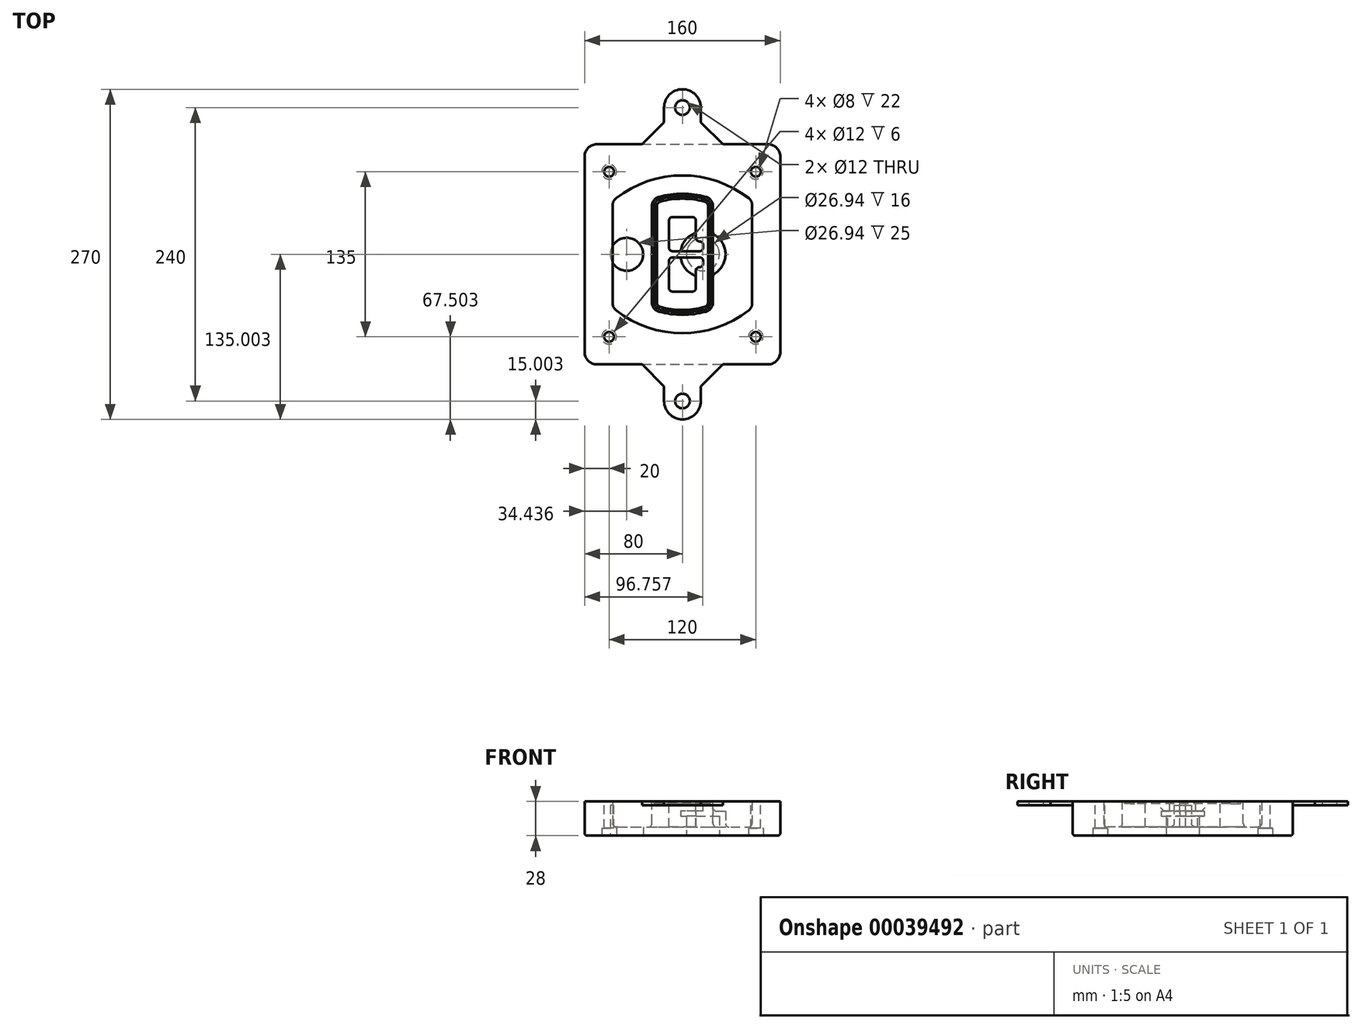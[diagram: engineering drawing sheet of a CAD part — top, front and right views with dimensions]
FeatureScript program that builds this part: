
annotation { "Feature Type Name" : "Feature", "Feature Type Description" : "" }
export const myFeature = defineFeature(function(context is Context, id is Id, definition is map)
    precondition{}
    {
        {
            var Q0;
            Q0=qCreatedBy(makeId("Top.planeOp"),FACE);
            var sketch = newSketch(context, id + "F0", { "sketchPlane" : qUnion([Q0])});
            skPoint(sketch, "E0.rect.middle", {"position": v(0, 0) * mm});
            skLineSegment(sketch, "E1.bottom", {"start": v(24.05, 28.38) * mm, "end": v(164.05, 28.38) * mm});
            skLineSegment(sketch, "E1.top", {"start": v(24.05, 208.38) * mm, "end": v(164.05, 208.38) * mm});
            skLineSegment(sketch, "E1.left", {"start": v(14.05, 38.38) * mm, "end": v(14.05, 198.38) * mm});
            skLineSegment(sketch, "E1.right", {"start": v(174.05, 38.38) * mm, "end": v(174.05, 198.38) * mm});
            skLineSegment(sketch, "E2", {"start": v(14.05, 208.38) * mm, "end": v(174.05, 28.38) * mm, "construction": true});
            skLineSegment(sketch, "E3", {"start": v(174.05, 208.38) * mm, "end": v(14.05, 28.38) * mm, "construction": true});
            skCircle(sketch, "E4", {"center": v(34.05, 185.88) * mm, "radius": 4 * mm});
            skCircle(sketch, "E5", {"center": v(154.05, 185.88) * mm, "radius": 4 * mm});
            skCircle(sketch, "E6", {"center": v(154.05, 50.88) * mm, "radius": 4 * mm});
            skCircle(sketch, "E7", {"center": v(34.05, 50.88) * mm, "radius": 4 * mm});
            skLineSegment(sketch, "E8", {"start": v(34.05, 185.88) * mm, "end": v(154.05, 185.88) * mm, "construction": true});
            skLineSegment(sketch, "E9", {"start": v(154.05, 185.88) * mm, "end": v(154.05, 50.88) * mm, "construction": true});
            skLineSegment(sketch, "E10", {"start": v(154.05, 50.88) * mm, "end": v(34.05, 50.88) * mm, "construction": true});
            skLineSegment(sketch, "E11", {"start": v(34.05, 50.88) * mm, "end": v(34.05, 185.88) * mm, "construction": true});
            skLineSegment(sketch, "E12", {"start": v(34.05, 158.68) * mm, "end": v(34.05, 78.09) * mm});
            skLineSegment(sketch, "E13", {"start": v(154.05, 158.68) * mm, "end": v(154.05, 78.09) * mm});
            skArc(sketch, "E14", {"start": v(150.2, 166.56) * mm, "mid": v(94.05, 185.88) * mm, "end": v(37.9, 166.56) * mm});
            skArc(sketch, "E15", {"start": v(37.9, 70.2) * mm, "mid": v(94.05, 50.88) * mm, "end": v(150.2, 70.2) * mm});
            skLineSegment(sketch, "E16", {"start": v(34.05, 118.38) * mm, "end": v(154.05, 118.38) * mm, "construction": true});
            skPoint(sketch, "E17.visualSharp", {"position": v(34.05, 73.38) * mm});
            skArc(sketch, "E17.filletArc", {"start": v(34.05, 78.09) * mm, "mid": v(35.06, 73.7) * mm, "end": v(37.9, 70.2) * mm});
            skPoint(sketch, "E18.visualSharp", {"position": v(34.05, 163.38) * mm});
            skArc(sketch, "E18.filletArc", {"start": v(37.9, 166.56) * mm, "mid": v(35.06, 163.06) * mm, "end": v(34.05, 158.68) * mm});
            skPoint(sketch, "E19.visualSharp", {"position": v(154.05, 163.38) * mm});
            skArc(sketch, "E19.filletArc", {"start": v(154.05, 158.68) * mm, "mid": v(153.04, 163.06) * mm, "end": v(150.2, 166.56) * mm});
            skPoint(sketch, "E20.visualSharp", {"position": v(154.05, 73.38) * mm});
            skArc(sketch, "E20.filletArc", {"start": v(150.2, 70.2) * mm, "mid": v(153.04, 73.7) * mm, "end": v(154.05, 78.09) * mm});
            skPoint(sketch, "E21.visualSharp", {"position": v(14.05, 208.38) * mm});
            skArc(sketch, "E21.filletArc", {"start": v(24.05, 208.38) * mm, "mid": v(16.98, 205.45) * mm, "end": v(14.05, 198.38) * mm});
            skPoint(sketch, "E22.visualSharp", {"position": v(174.05, 208.38) * mm});
            skArc(sketch, "E22.filletArc", {"start": v(174.05, 198.38) * mm, "mid": v(171.12, 205.45) * mm, "end": v(164.05, 208.38) * mm});
            skPoint(sketch, "E23.visualSharp", {"position": v(174.05, 28.38) * mm});
            skArc(sketch, "E23.filletArc", {"start": v(164.05, 28.38) * mm, "mid": v(171.12, 31.31) * mm, "end": v(174.05, 38.38) * mm});
            skPoint(sketch, "E24.visualSharp", {"position": v(14.05, 28.38) * mm});
            skArc(sketch, "E24.filletArc", {"start": v(14.05, 38.38) * mm, "mid": v(16.98, 31.31) * mm, "end": v(24.05, 28.38) * mm});
            skArc(sketch, "E25.0", {"start": v(151.05, 158.68) * mm, "mid": v(150.34, 161.75) * mm, "end": v(148.36, 164.2) * mm});
            skLineSegment(sketch, "E25.1", {"start": v(151.05, 158.68) * mm, "end": v(151.05, 78.09) * mm});
            skArc(sketch, "E25.2", {"start": v(148.36, 72.57) * mm, "mid": v(150.34, 75.02) * mm, "end": v(151.05, 78.09) * mm});
            skArc(sketch, "E25.3", {"start": v(39.74, 72.57) * mm, "mid": v(94.05, 53.88) * mm, "end": v(148.36, 72.57) * mm});
            skArc(sketch, "E25.4", {"start": v(37.05, 78.09) * mm, "mid": v(37.76, 75.02) * mm, "end": v(39.74, 72.57) * mm});
            skArc(sketch, "E25.5", {"start": v(148.36, 164.2) * mm, "mid": v(94.05, 182.88) * mm, "end": v(39.74, 164.2) * mm});
            skLineSegment(sketch, "E25.6", {"start": v(37.05, 158.68) * mm, "end": v(37.05, 78.09) * mm});
            skArc(sketch, "E25.7", {"start": v(39.74, 164.2) * mm, "mid": v(37.76, 161.75) * mm, "end": v(37.05, 158.68) * mm});
            skArc(sketch, "E26.0", {"start": v(35.43, 169.71) * mm, "mid": v(31.47, 164.82) * mm, "end": v(30.05, 158.68) * mm});
            skArc(sketch, "E26.1", {"start": v(152.67, 169.71) * mm, "mid": v(94.05, 189.88) * mm, "end": v(35.43, 169.71) * mm});
            skArc(sketch, "E26.2", {"start": v(158.05, 158.68) * mm, "mid": v(156.63, 164.82) * mm, "end": v(152.67, 169.71) * mm});
            skLineSegment(sketch, "E26.3", {"start": v(158.05, 158.68) * mm, "end": v(158.05, 78.09) * mm});
            skArc(sketch, "E26.4", {"start": v(152.67, 67.05) * mm, "mid": v(156.63, 71.95) * mm, "end": v(158.05, 78.09) * mm});
            skLineSegment(sketch, "E26.5", {"start": v(30.05, 158.68) * mm, "end": v(30.05, 78.09) * mm});
            skArc(sketch, "E26.6", {"start": v(35.43, 67.05) * mm, "mid": v(94.05, 46.88) * mm, "end": v(152.67, 67.05) * mm});
            skArc(sketch, "E26.7", {"start": v(30.05, 78.09) * mm, "mid": v(31.47, 71.95) * mm, "end": v(35.43, 67.05) * mm});
            skSolve(sketch);
        }
        {
            var Q0;
            Q0=makeQuery(id+"F0.imprint","IMPRINT",FACE,{"disambiguationData":[TD([[makeQuery(id+"F0.imprint","IMPRINT",EDGE,{"derivedFrom":sQuery(id+"F0.wireOp",EDGE,"E1.bottom")}),1.0]])]});
            var Q1;
            Q1=makeQuery(id+"F0.imprint","IMPRINT",FACE,{"disambiguationData":[TD([[makeQuery(id+"F0.imprint","IMPRINT",EDGE,{"derivedFrom":sQuery(id+"F0.wireOp",EDGE,"E12")}),1.0]])]});
            var Q2;
            Q2=makeQuery(id+"F0.imprint","IMPRINT",FACE,{"disambiguationData":[TD([[makeQuery(id+"F0.imprint","IMPRINT",EDGE,{"derivedFrom":sQuery(id+"F0.wireOp",EDGE,"E25.0")}),1.0]])]});
            var Q3;
            Q3=makeQuery(id+"F0.imprint","IMPRINT",FACE,{"disambiguationData":[TD([[makeQuery(id+"F0.imprint","IMPRINT",EDGE,{"derivedFrom":sQuery(id+"F0.wireOp",EDGE,"E12")}),-1.0]])]});
            extrude(context, id + "F1", {"entities" : qUnion([Q0, Q1, Q2, Q3]), "oppositeDirection" : true, "depth" : 25 * mm});
        }
        {
            var Q0;
            Q0=makeQuery(id+"F0.imprint","IMPRINT",FACE,{"disambiguationData":[TD([[makeQuery(id+"F0.imprint","IMPRINT",EDGE,{"derivedFrom":sQuery(id+"F0.wireOp",EDGE,"E12")}),1.0]])]});
            extrude(context, id + "F2", {"entities" : qUnion([Q0]), "operationType" : NewBodyOperationType.ADD, "depth" : 3 * mm});
        }
        {
            var Q0;
            Q0=makeQuery(id+"F0.imprint","IMPRINT",FACE,{"disambiguationData":[TD([[makeQuery(id+"F0.imprint","IMPRINT",EDGE,{"derivedFrom":sQuery(id+"F0.wireOp",EDGE,"E25.0")}),1.0]])]});
            extrude(context, id + "F3", {"entities" : qUnion([Q0]), "operationType" : NewBodyOperationType.REMOVE, "oppositeDirection" : true, "depth" : 18 * mm});
        }
        {
            var Q0;
            Q0=makeQuery(id+"F2.opExtrude","CAP_FACE",FACE,{"disambiguationData":[OSD([sQuery(id+"F0.wireOp",EDGE,"E12"),sQuery(id+"F0.wireOp",EDGE,"E13"),sQuery(id+"F0.wireOp",EDGE,"E14"),sQuery(id+"F0.wireOp",EDGE,"E15"),sQuery(id+"F0.wireOp",EDGE,"E17.filletArc"),sQuery(id+"F0.wireOp",EDGE,"E18.filletArc"),sQuery(id+"F0.wireOp",EDGE,"E19.filletArc"),sQuery(id+"F0.wireOp",EDGE,"E20.filletArc"),sQuery(id+"F0.wireOp",EDGE,"E25.0"),sQuery(id+"F0.wireOp",EDGE,"E25.1"),sQuery(id+"F0.wireOp",EDGE,"E25.2"),sQuery(id+"F0.wireOp",EDGE,"E25.3"),sQuery(id+"F0.wireOp",EDGE,"E25.4"),sQuery(id+"F0.wireOp",EDGE,"E25.5"),sQuery(id+"F0.wireOp",EDGE,"E25.6"),sQuery(id+"F0.wireOp",EDGE,"E25.7")])],"isStart":false});
            var sketch = newSketch(context, id + "F4", { "sketchPlane" : qUnion([Q0])});
            skArc(sketch, "E27.0", {"start": v(74.97, 71.41) * mm, "mid": v(94.05, 68.88) * mm, "end": v(113.13, 71.41) * mm});
            skArc(sketch, "E28.0", {"start": v(113.13, 165.35) * mm, "mid": v(94.05, 167.88) * mm, "end": v(74.97, 165.35) * mm});
            skLineSegment(sketch, "E29", {"start": v(69.05, 157.63) * mm, "end": v(69.05, 79.14) * mm});
            skLineSegment(sketch, "E30", {"start": v(119.05, 157.63) * mm, "end": v(119.05, 79.14) * mm});
            skLineSegment(sketch, "E31", {"start": v(69.05, 163.48) * mm, "end": v(119.05, 163.48) * mm, "construction": true});
            skLineSegment(sketch, "E32", {"start": v(69.05, 73.28) * mm, "end": v(119.05, 73.28) * mm, "construction": true});
            skPoint(sketch, "E33.visualSharp", {"position": v(69.05, 163.48) * mm});
            skArc(sketch, "E33.filletArc", {"start": v(74.97, 165.35) * mm, "mid": v(70.7, 162.5) * mm, "end": v(69.05, 157.63) * mm});
            skPoint(sketch, "E34.visualSharp", {"position": v(119.05, 163.48) * mm});
            skArc(sketch, "E34.filletArc", {"start": v(119.05, 157.63) * mm, "mid": v(117.4, 162.5) * mm, "end": v(113.13, 165.35) * mm});
            skPoint(sketch, "E35.visualSharp", {"position": v(119.05, 73.28) * mm});
            skArc(sketch, "E35.filletArc", {"start": v(113.13, 71.41) * mm, "mid": v(117.4, 74.27) * mm, "end": v(119.05, 79.14) * mm});
            skPoint(sketch, "E36.visualSharp", {"position": v(69.05, 73.28) * mm});
            skArc(sketch, "E36.filletArc", {"start": v(69.05, 79.14) * mm, "mid": v(70.7, 74.27) * mm, "end": v(74.97, 71.41) * mm});
            skArc(sketch, "E37.0", {"start": v(148.36, 164.2) * mm, "mid": v(94.05, 182.88) * mm, "end": v(39.74, 164.2) * mm});
            skArc(sketch, "E37.1", {"start": v(39.74, 164.2) * mm, "mid": v(37.76, 161.75) * mm, "end": v(37.05, 158.68) * mm});
            skLineSegment(sketch, "E37.2", {"start": v(37.05, 158.68) * mm, "end": v(37.05, 78.09) * mm});
            skArc(sketch, "E37.3", {"start": v(37.05, 78.09) * mm, "mid": v(37.76, 75.02) * mm, "end": v(39.74, 72.57) * mm});
            skArc(sketch, "E37.4", {"start": v(39.74, 72.57) * mm, "mid": v(94.05, 53.88) * mm, "end": v(148.36, 72.57) * mm});
            skArc(sketch, "E37.5", {"start": v(148.36, 72.57) * mm, "mid": v(150.34, 75.02) * mm, "end": v(151.05, 78.09) * mm});
            skLineSegment(sketch, "E37.6", {"start": v(151.05, 158.68) * mm, "end": v(151.05, 78.09) * mm});
            skArc(sketch, "E37.7", {"start": v(151.05, 158.68) * mm, "mid": v(150.34, 161.75) * mm, "end": v(148.36, 164.2) * mm});
            skLineSegment(sketch, "E38.0", {"start": v(117.05, 157.63) * mm, "end": v(117.05, 79.14) * mm});
            skArc(sketch, "E38.1", {"start": v(112.61, 73.34) * mm, "mid": v(115.81, 75.49) * mm, "end": v(117.05, 79.14) * mm});
            skArc(sketch, "E38.2", {"start": v(75.49, 73.34) * mm, "mid": v(94.05, 70.88) * mm, "end": v(112.61, 73.34) * mm});
            skArc(sketch, "E38.3", {"start": v(71.05, 79.14) * mm, "mid": v(72.29, 75.49) * mm, "end": v(75.49, 73.34) * mm});
            skLineSegment(sketch, "E38.4", {"start": v(71.05, 157.63) * mm, "end": v(71.05, 79.14) * mm});
            skArc(sketch, "E38.5", {"start": v(117.05, 157.63) * mm, "mid": v(115.81, 161.28) * mm, "end": v(112.61, 163.42) * mm});
            skArc(sketch, "E38.6", {"start": v(75.49, 163.42) * mm, "mid": v(72.29, 161.28) * mm, "end": v(71.05, 157.63) * mm});
            skArc(sketch, "E38.7", {"start": v(112.61, 163.42) * mm, "mid": v(94.05, 165.88) * mm, "end": v(75.49, 163.42) * mm});
            skArc(sketch, "E39.0", {"start": v(115.05, 157.63) * mm, "mid": v(114.23, 160.06) * mm, "end": v(112.1, 161.5) * mm});
            skLineSegment(sketch, "E39.1", {"start": v(115.05, 157.63) * mm, "end": v(115.05, 79.14) * mm});
            skArc(sketch, "E39.2", {"start": v(112.1, 75.27) * mm, "mid": v(114.23, 76.7) * mm, "end": v(115.05, 79.14) * mm});
            skArc(sketch, "E39.3", {"start": v(76, 75.27) * mm, "mid": v(94.05, 72.88) * mm, "end": v(112.1, 75.27) * mm});
            skArc(sketch, "E39.4", {"start": v(73.05, 79.14) * mm, "mid": v(73.87, 76.7) * mm, "end": v(76, 75.27) * mm});
            skArc(sketch, "E39.5", {"start": v(112.1, 161.5) * mm, "mid": v(94.05, 163.88) * mm, "end": v(76, 161.5) * mm});
            skLineSegment(sketch, "E39.6", {"start": v(73.05, 157.63) * mm, "end": v(73.05, 79.14) * mm});
            skArc(sketch, "E39.7", {"start": v(76, 161.5) * mm, "mid": v(73.87, 160.06) * mm, "end": v(73.05, 157.63) * mm});
            skLineSegment(sketch, "E40", {"start": v(69.05, 118.38) * mm, "end": v(119.05, 118.38) * mm, "construction": true});
            skLineSegment(sketch, "E41", {"start": v(83.05, 123.88) * mm, "end": v(83.05, 145.88) * mm});
            skLineSegment(sketch, "E42", {"start": v(86.05, 148.88) * mm, "end": v(102.05, 148.88) * mm});
            skLineSegment(sketch, "E43", {"start": v(105.05, 145.88) * mm, "end": v(105.05, 131.88) * mm});
            skLineSegment(sketch, "E44", {"start": v(108.05, 128.88) * mm, "end": v(108.05, 128.88) * mm});
            skLineSegment(sketch, "E45", {"start": v(111.05, 125.88) * mm, "end": v(111.05, 123.88) * mm});
            skLineSegment(sketch, "E46", {"start": v(108.05, 120.88) * mm, "end": v(86.05, 120.88) * mm});
            skPoint(sketch, "E47.visualSharp", {"position": v(83.05, 148.88) * mm});
            skArc(sketch, "E47.filletArc", {"start": v(86.05, 148.88) * mm, "mid": v(83.93, 148) * mm, "end": v(83.05, 145.88) * mm});
            skPoint(sketch, "E48.visualSharp", {"position": v(105.05, 148.88) * mm});
            skArc(sketch, "E48.filletArc", {"start": v(105.05, 145.88) * mm, "mid": v(104.17, 148) * mm, "end": v(102.05, 148.88) * mm});
            skPoint(sketch, "E49.visualSharp", {"position": v(105.05, 128.88) * mm});
            skArc(sketch, "E49.filletArc", {"start": v(105.05, 131.88) * mm, "mid": v(105.93, 129.76) * mm, "end": v(108.05, 128.88) * mm});
            skPoint(sketch, "E50.visualSharp", {"position": v(111.05, 128.88) * mm});
            skArc(sketch, "E50.filletArc", {"start": v(111.05, 125.88) * mm, "mid": v(110.17, 128) * mm, "end": v(108.05, 128.88) * mm});
            skPoint(sketch, "E51.visualSharp", {"position": v(111.05, 120.88) * mm});
            skArc(sketch, "E51.filletArc", {"start": v(108.05, 120.88) * mm, "mid": v(110.17, 121.76) * mm, "end": v(111.05, 123.88) * mm});
            skPoint(sketch, "E52.visualSharp", {"position": v(83.05, 120.88) * mm});
            skArc(sketch, "E52.filletArc", {"start": v(83.05, 123.88) * mm, "mid": v(83.93, 121.76) * mm, "end": v(86.05, 120.88) * mm});
            skLineSegment(sketch, "E53.0.MirrorCS", {"start": v(108.05, 115.88) * mm, "end": v(86.05, 115.88) * mm});
            skArc(sketch, "E54.0.MirrorCS", {"start": v(83.05, 112.88) * mm, "mid": v(83.93, 115) * mm, "end": v(86.05, 115.88) * mm});
            skLineSegment(sketch, "E55.0.MirrorCS", {"start": v(83.05, 112.88) * mm, "end": v(83.05, 90.88) * mm});
            skArc(sketch, "E56.0.MirrorCS", {"start": v(86.05, 87.88) * mm, "mid": v(83.93, 88.76) * mm, "end": v(83.05, 90.88) * mm});
            skLineSegment(sketch, "E57.0.MirrorCS", {"start": v(86.05, 87.88) * mm, "end": v(102.05, 87.88) * mm});
            skArc(sketch, "E58.0.MirrorCS", {"start": v(105.05, 90.88) * mm, "mid": v(104.17, 88.76) * mm, "end": v(102.05, 87.88) * mm});
            skLineSegment(sketch, "E59.0.MirrorCS", {"start": v(105.05, 90.88) * mm, "end": v(105.05, 104.88) * mm});
            skArc(sketch, "E60.0.MirrorCS", {"start": v(105.05, 104.88) * mm, "mid": v(105.93, 107) * mm, "end": v(108.05, 107.88) * mm});
            skArc(sketch, "E61.0.MirrorCS", {"start": v(111.05, 110.88) * mm, "mid": v(110.17, 108.76) * mm, "end": v(108.05, 107.88) * mm});
            skLineSegment(sketch, "E62.0.MirrorCS", {"start": v(111.05, 110.88) * mm, "end": v(111.05, 112.88) * mm});
            skArc(sketch, "E63.0.MirrorCS", {"start": v(108.05, 115.88) * mm, "mid": v(110.17, 115) * mm, "end": v(111.05, 112.88) * mm});
            skSolve(sketch);
        }
        {
            var Q0;
            Q0=makeQuery(id+"F4.imprint","IMPRINT",FACE,{"disambiguationData":[TD([[makeQuery(id+"F4.imprint","IMPRINT",EDGE,{"derivedFrom":sQuery(id+"F4.wireOp",EDGE,"E27.0")}),1.0]])]});
            var Q1;
            Q1=makeQuery(id+"F4.imprint","IMPRINT",FACE,{"disambiguationData":[TD([[makeQuery(id+"F4.imprint","IMPRINT",EDGE,{"derivedFrom":sQuery(id+"F4.wireOp",EDGE,"E38.0")}),-1.0]])]});
            var Q2;
            Q2=makeQuery(id+"F4.imprint","IMPRINT",FACE,{"disambiguationData":[TD([[makeQuery(id+"F4.imprint","IMPRINT",EDGE,{"derivedFrom":sQuery(id+"F4.wireOp",EDGE,"E39.0")}),1.0]])]});
            extrude(context, id + "F5", {"entities" : qUnion([Q0, Q1, Q2]), "operationType" : NewBodyOperationType.ADD, "endBound" : BoundingType.UP_TO_NEXT, "oppositeDirection" : true, "depth" : 25 * mm});
        }
        {
            var Q0;
            Q0=makeQuery(id+"F4.imprint","IMPRINT",FACE,{"disambiguationData":[TD([[makeQuery(id+"F4.imprint","IMPRINT",EDGE,{"derivedFrom":sQuery(id+"F4.wireOp",EDGE,"E38.0")}),-1.0]])]});
            extrude(context, id + "F6", {"entities" : qUnion([Q0]), "operationType" : NewBodyOperationType.REMOVE, "oppositeDirection" : true, "depth" : 2 * mm});
        }
        {
            var Q0;
            Q0=makeQuery(id+"F1.opExtrude","CAP_FACE",FACE,{"disambiguationData":[OSD([sQuery(id+"F0.wireOp",EDGE,"E1.bottom"),sQuery(id+"F0.wireOp",EDGE,"E1.top"),sQuery(id+"F0.wireOp",EDGE,"E1.left"),sQuery(id+"F0.wireOp",EDGE,"E1.right"),sQuery(id+"F0.wireOp",EDGE,"E4"),sQuery(id+"F0.wireOp",EDGE,"E5"),sQuery(id+"F0.wireOp",EDGE,"E6"),sQuery(id+"F0.wireOp",EDGE,"E7"),sQuery(id+"F0.wireOp",EDGE,"E21.filletArc"),sQuery(id+"F0.wireOp",EDGE,"E22.filletArc"),sQuery(id+"F0.wireOp",EDGE,"E23.filletArc"),sQuery(id+"F0.wireOp",EDGE,"E24.filletArc")])],"isStart":false});
            var sketch = newSketch(context, id + "F7", { "sketchPlane" : qUnion([Q0])});
            skCircle(sketch, "E64", {"center": v(110.8, -118.38) * mm, "radius": 13.47 * mm});
            skCircle(sketch, "E65", {"center": v(48.49, -118.38) * mm, "radius": 13.47 * mm});
            skLineSegment(sketch, "E66", {"start": v(174.05, -118.38) * mm, "end": v(14.05, -118.38) * mm});
            skCircle(sketch, "E67", {"center": v(110.8, -118.38) * mm, "radius": 18.47 * mm});
            skCircle(sketch, "E68", {"center": v(154.05, -185.88) * mm, "radius": 6 * mm});
            skCircle(sketch, "E69", {"center": v(34.05, -185.88) * mm, "radius": 6 * mm});
            skCircle(sketch, "E70", {"center": v(34.05, -50.88) * mm, "radius": 6 * mm});
            skCircle(sketch, "E71", {"center": v(154.05, -50.88) * mm, "radius": 6 * mm});
            skSolve(sketch);
        }
        {
            var Q0;
            {var subQ1=sQuery(id+"F7.wireOp",EDGE,"E66");var subQ4=sQuery(id+"F7.wireOp",EDGE,"E64");var subQ6=makeQuery(id+"F7.imprint","INTERSECT",VERTEX,{"disambiguationData":[OD(0.0)],"derivedFrom":[subQ4,subQ1]});Q0=makeQuery(id+"F7.imprint","IMPRINT",FACE,{"disambiguationData":[TD([[makeQuery(id+"F7.imprint","IMPRINT",EDGE,{"disambiguationData":[TD([[subQ6,-1.0]])],"derivedFrom":subQ4}),-1.0]])]});}
            var Q1;
            {var subQ0=sQuery(id+"F7.wireOp",EDGE,"E66");var subQ1=sQuery(id+"F7.wireOp",EDGE,"E64");var subQ3=makeQuery(id+"F7.imprint","INTERSECT",VERTEX,{"disambiguationData":[OD(0.0)],"derivedFrom":[subQ1,subQ0]});Q1=makeQuery(id+"F7.imprint","IMPRINT",FACE,{"disambiguationData":[TD([[makeQuery(id+"F7.imprint","IMPRINT",EDGE,{"disambiguationData":[TD([[subQ3,-1.0]])],"derivedFrom":subQ1}),1.0]])]});}
            var Q2;
            {var subQ0=sQuery(id+"F7.wireOp",EDGE,"E66");var subQ1=sQuery(id+"F7.wireOp",EDGE,"E64");var subQ3=makeQuery(id+"F7.imprint","INTERSECT",VERTEX,{"disambiguationData":[OD(0.0)],"derivedFrom":[subQ1,subQ0]});Q2=makeQuery(id+"F7.imprint","IMPRINT",FACE,{"disambiguationData":[TD([[makeQuery(id+"F7.imprint","IMPRINT",EDGE,{"disambiguationData":[TD([[subQ3,1.0]])],"derivedFrom":subQ1}),1.0]])]});}
            var Q3;
            {var subQ1=sQuery(id+"F7.wireOp",EDGE,"E66");var subQ4=sQuery(id+"F7.wireOp",EDGE,"E64");var subQ6=makeQuery(id+"F7.imprint","INTERSECT",VERTEX,{"disambiguationData":[OD(0.0)],"derivedFrom":[subQ4,subQ1]});Q3=makeQuery(id+"F7.imprint","IMPRINT",FACE,{"disambiguationData":[TD([[makeQuery(id+"F7.imprint","IMPRINT",EDGE,{"disambiguationData":[TD([[subQ6,1.0]])],"derivedFrom":subQ4}),-1.0]])]});}
            extrude(context, id + "F8", {"entities" : qUnion([Q0, Q1, Q2, Q3]), "operationType" : NewBodyOperationType.ADD, "oppositeDirection" : true, "depth" : 20 * mm});
        }
        {
            var Q0;
            {var subQ0=sQuery(id+"F7.wireOp",EDGE,"E66");var subQ1=sQuery(id+"F7.wireOp",EDGE,"E64");var subQ3=makeQuery(id+"F7.imprint","INTERSECT",VERTEX,{"disambiguationData":[OD(0.0)],"derivedFrom":[subQ1,subQ0]});Q0=makeQuery(id+"F7.imprint","IMPRINT",FACE,{"disambiguationData":[TD([[makeQuery(id+"F7.imprint","IMPRINT",EDGE,{"disambiguationData":[TD([[subQ3,-1.0]])],"derivedFrom":subQ1}),1.0]])]});}
            var Q1;
            {var subQ0=sQuery(id+"F7.wireOp",EDGE,"E66");var subQ1=sQuery(id+"F7.wireOp",EDGE,"E64");var subQ3=makeQuery(id+"F7.imprint","INTERSECT",VERTEX,{"disambiguationData":[OD(0.0)],"derivedFrom":[subQ1,subQ0]});Q1=makeQuery(id+"F7.imprint","IMPRINT",FACE,{"disambiguationData":[TD([[makeQuery(id+"F7.imprint","IMPRINT",EDGE,{"disambiguationData":[TD([[subQ3,1.0]])],"derivedFrom":subQ1}),1.0]])]});}
            extrude(context, id + "F9", {"entities" : qUnion([Q0, Q1]), "operationType" : NewBodyOperationType.REMOVE, "oppositeDirection" : true, "depth" : 16 * mm});
        }
        {
            var Q0;
            {var subQ0=sQuery(id+"F7.wireOp",EDGE,"E66");var subQ1=sQuery(id+"F7.wireOp",EDGE,"E65");var subQ3=makeQuery(id+"F7.imprint","INTERSECT",VERTEX,{"disambiguationData":[OD(0.0)],"derivedFrom":[subQ1,subQ0]});Q0=makeQuery(id+"F7.imprint","IMPRINT",FACE,{"disambiguationData":[TD([[makeQuery(id+"F7.imprint","IMPRINT",EDGE,{"disambiguationData":[TD([[subQ3,-1.0]])],"derivedFrom":subQ1}),1.0]])]});}
            var Q1;
            {var subQ0=sQuery(id+"F7.wireOp",EDGE,"E66");var subQ1=sQuery(id+"F7.wireOp",EDGE,"E65");var subQ3=makeQuery(id+"F7.imprint","INTERSECT",VERTEX,{"disambiguationData":[OD(0.0)],"derivedFrom":[subQ1,subQ0]});Q1=makeQuery(id+"F7.imprint","IMPRINT",FACE,{"disambiguationData":[TD([[makeQuery(id+"F7.imprint","IMPRINT",EDGE,{"disambiguationData":[TD([[subQ3,1.0]])],"derivedFrom":subQ1}),1.0]])]});}
            extrude(context, id + "F10", {"entities" : qUnion([Q0, Q1]), "operationType" : NewBodyOperationType.REMOVE, "oppositeDirection" : true, "depth" : 25 * mm});
        }
        {
            var Q0;
            Q0=makeQuery(id+"F7.imprint","IMPRINT",FACE,{"disambiguationData":[TD([[makeQuery(id+"F7.imprint","IMPRINT",EDGE,{"derivedFrom":sQuery(id+"F7.wireOp",EDGE,"E68")}),1.0]])]});
            var Q1;
            Q1=makeQuery(id+"F7.imprint","IMPRINT",FACE,{"disambiguationData":[TD([[makeQuery(id+"F7.imprint","IMPRINT",EDGE,{"derivedFrom":makeQuery(id+"F1.opExtrude","CAP_EDGE",EDGE,{"disambiguationData":[OSD([sQuery(id+"F0.wireOp",EDGE,"E5")])],"isStart":false})}),-1.0]])]});
            var Q2;
            Q2=makeQuery(id+"F7.imprint","IMPRINT",FACE,{"disambiguationData":[TD([[makeQuery(id+"F7.imprint","IMPRINT",EDGE,{"derivedFrom":sQuery(id+"F7.wireOp",EDGE,"E69")}),1.0]])]});
            var Q3;
            Q3=makeQuery(id+"F7.imprint","IMPRINT",FACE,{"disambiguationData":[TD([[makeQuery(id+"F7.imprint","IMPRINT",EDGE,{"derivedFrom":makeQuery(id+"F1.opExtrude","CAP_EDGE",EDGE,{"disambiguationData":[OSD([sQuery(id+"F0.wireOp",EDGE,"E4")])],"isStart":false})}),-1.0]])]});
            var Q4;
            Q4=makeQuery(id+"F7.imprint","IMPRINT",FACE,{"disambiguationData":[TD([[makeQuery(id+"F7.imprint","IMPRINT",EDGE,{"derivedFrom":sQuery(id+"F7.wireOp",EDGE,"E70")}),1.0]])]});
            var Q5;
            Q5=makeQuery(id+"F7.imprint","IMPRINT",FACE,{"disambiguationData":[TD([[makeQuery(id+"F7.imprint","IMPRINT",EDGE,{"derivedFrom":makeQuery(id+"F1.opExtrude","CAP_EDGE",EDGE,{"disambiguationData":[OSD([sQuery(id+"F0.wireOp",EDGE,"E7")])],"isStart":false})}),-1.0]])]});
            var Q6;
            Q6=makeQuery(id+"F7.imprint","IMPRINT",FACE,{"disambiguationData":[TD([[makeQuery(id+"F7.imprint","IMPRINT",EDGE,{"derivedFrom":sQuery(id+"F7.wireOp",EDGE,"E71")}),1.0]])]});
            var Q7;
            Q7=makeQuery(id+"F7.imprint","IMPRINT",FACE,{"disambiguationData":[TD([[makeQuery(id+"F7.imprint","IMPRINT",EDGE,{"derivedFrom":makeQuery(id+"F1.opExtrude","CAP_EDGE",EDGE,{"disambiguationData":[OSD([sQuery(id+"F0.wireOp",EDGE,"E6")])],"isStart":false})}),-1.0]])]});
            extrude(context, id + "F11", {"entities" : qUnion([Q0, Q1, Q2, Q3, Q4, Q5, Q6, Q7]), "operationType" : NewBodyOperationType.REMOVE, "oppositeDirection" : true, "depth" : 6 * mm});
        }
        {
            var Q0;
            Q0=makeQuery(id+"F9.boolean.opBoolean","COPY",FACE,{"derivedFrom":makeQuery(id+"F9.opExtrude","CAP_FACE",FACE,{"disambiguationData":[OSD([sQuery(id+"F7.wireOp",EDGE,"E64")])],"isStart":false})});
            var sketch = newSketch(context, id + "F12", { "sketchPlane" : qUnion([Q0])});
            skArc(sketch, "E72.0", {"start": v(105.05, -100.83) * mm, "mid": v(96.62, -106.56) * mm, "end": v(92.5, -115.88) * mm});
            skArc(sketch, "E72.1", {"start": v(92.5, -120.88) * mm, "mid": v(96.62, -130.2) * mm, "end": v(105.05, -135.93) * mm});
            skLineSegment(sketch, "E73", {"start": v(92.5, -120.88) * mm, "end": v(108.05, -120.88) * mm});
            skLineSegment(sketch, "E74.0", {"start": v(108.05, -115.88) * mm, "end": v(92.5, -115.88) * mm});
            skArc(sketch, "E74.1", {"start": v(108.05, -115.88) * mm, "mid": v(110.17, -115) * mm, "end": v(111.05, -112.88) * mm});
            skLineSegment(sketch, "E74.2", {"start": v(111.05, -110.88) * mm, "end": v(111.05, -112.88) * mm});
            skArc(sketch, "E74.3", {"start": v(111.05, -110.88) * mm, "mid": v(110.17, -108.76) * mm, "end": v(108.05, -107.88) * mm});
            skArc(sketch, "E74.4", {"start": v(105.05, -104.88) * mm, "mid": v(105.93, -107) * mm, "end": v(108.05, -107.88) * mm});
            skLineSegment(sketch, "E74.5", {"start": v(105.05, -100.83) * mm, "end": v(105.05, -104.88) * mm});
            skLineSegment(sketch, "E74.7", {"start": v(108.05, -120.88) * mm, "end": v(92.5, -120.88) * mm});
            skArc(sketch, "E74.8", {"start": v(108.05, -120.88) * mm, "mid": v(110.17, -121.76) * mm, "end": v(111.05, -123.88) * mm});
            skLineSegment(sketch, "E74.9", {"start": v(111.05, -125.88) * mm, "end": v(111.05, -123.88) * mm});
            skArc(sketch, "E74.10", {"start": v(111.05, -125.88) * mm, "mid": v(110.17, -128) * mm, "end": v(108.05, -128.88) * mm});
            skArc(sketch, "E74.11", {"start": v(105.05, -131.88) * mm, "mid": v(105.93, -129.76) * mm, "end": v(108.05, -128.88) * mm});
            skLineSegment(sketch, "E74.12", {"start": v(105.05, -135.93) * mm, "end": v(105.05, -131.88) * mm});
            skPoint(sketch, "E75.orphan", {"position": v(105.05, -145.88) * mm});
            skPoint(sketch, "E76.orphan", {"position": v(86.05, -120.88) * mm});
            skPoint(sketch, "E77.orphan", {"position": v(86.05, -115.88) * mm});
            skPoint(sketch, "E78.orphan", {"position": v(105.05, -90.88) * mm});
            skSolve(sketch);
        }
        {
            var Q0;
            {var subQ7=sQuery(id+"F12.wireOp",EDGE,"E72.0");var subQ14=sQuery(id+"F12.wireOp",EDGE,"E72.1");var subQ16=sQuery(id+"F12.wireOp",EDGE,"E74.1");var subQ18=sQuery(id+"F12.wireOp",EDGE,"E74.8");Q0=qUnion([makeQuery(id+"F12.imprint","IMPRINT",FACE,{"disambiguationData":[TD([[makeQuery(id+"F12.imprint","IMPRINT",EDGE,{"derivedFrom":subQ7}),1.0]])]}),makeQuery(id+"F12.imprint","IMPRINT",FACE,{"disambiguationData":[TD([[makeQuery(id+"F12.imprint","IMPRINT",EDGE,{"derivedFrom":subQ14}),1.0]])]}),makeQuery(id+"F12.imprint","IMPRINT",FACE,{"disambiguationData":[TD([[makeQuery(id+"F12.imprint","IMPRINT",EDGE,{"derivedFrom":subQ16}),1.0]])]}),makeQuery(id+"F12.imprint","IMPRINT",FACE,{"disambiguationData":[TD([[makeQuery(id+"F12.imprint","IMPRINT",EDGE,{"derivedFrom":subQ18}),-1.0]])]})]);}
            var Q1;
            Q1=makeQuery(id+"F5.boolean.opBoolean","SPLIT",FACE,{"disambiguationData":[TD([makeQuery(id+"F5.opExtrude","SWEPT_FACE",FACE,{"disambiguationData":[OSD([sQuery(id+"F4.wireOp",EDGE,"E41")])]})])],"derivedFrom":makeQuery(id+"F3.boolean.opBoolean","COPY",FACE,{"derivedFrom":makeQuery(id+"F3.opExtrude","CAP_FACE",FACE,{"disambiguationData":[OSD([sQuery(id+"F0.wireOp",EDGE,"E25.0"),sQuery(id+"F0.wireOp",EDGE,"E25.1"),sQuery(id+"F0.wireOp",EDGE,"E25.2"),sQuery(id+"F0.wireOp",EDGE,"E25.3"),sQuery(id+"F0.wireOp",EDGE,"E25.4"),sQuery(id+"F0.wireOp",EDGE,"E25.5"),sQuery(id+"F0.wireOp",EDGE,"E25.6"),sQuery(id+"F0.wireOp",EDGE,"E25.7")])],"isStart":false})})});
            extrude(context, id + "F13", {"entities" : qUnion([Q0]), "operationType" : NewBodyOperationType.REMOVE, "endBound" : BoundingType.UP_TO_SURFACE, "endBoundEntityFace" : qUnion([Q1]), "depth" : 25 * mm});
        }
        {
            var Q0;
            Q0=makeQuery(id+"F3.boolean.opBoolean","COPY",EDGE,{"derivedFrom":makeQuery(id+"F3.opExtrude","CAP_EDGE",EDGE,{"disambiguationData":[OSD([sQuery(id+"F0.wireOp",EDGE,"E25.6")])],"isStart":false})});
            var Q1;
            Q1=makeQuery(id+"F8.boolean.opBoolean","INTERSECT",EDGE,{"derivedFrom":[makeQuery(id+"F5.opExtrude","SWEPT_FACE",FACE,{"disambiguationData":[OSD([sQuery(id+"F4.wireOp",EDGE,"E30")])]}),makeQuery(id+"F8.opExtrude","CAP_FACE",FACE,{"disambiguationData":[OSD([sQuery(id+"F7.wireOp",EDGE,"E67")])],"isStart":false})]});
            var Q2;
            Q2=makeQuery(id+"F8.boolean.opBoolean","INTERSECT",EDGE,{"disambiguationData":[OD(1.0)],"derivedFrom":[makeQuery(id+"F5.opExtrude","SWEPT_FACE",FACE,{"disambiguationData":[OSD([sQuery(id+"F4.wireOp",EDGE,"E30")])]}),makeQuery(id+"F8.opExtrude","SWEPT_FACE",FACE,{"disambiguationData":[OSD([sQuery(id+"F7.wireOp",EDGE,"E67")])]})]});
            var Q3;
            {var subQ0=sQuery(id+"F4.wireOp",EDGE,"E30");Q3=makeQuery(id+"F8.boolean.opBoolean","SPLIT",EDGE,{"disambiguationData":[TD([makeQuery(id+"F5.opExtrude","SWEPT_FACE",FACE,{"disambiguationData":[OSD([sQuery(id+"F4.wireOp",EDGE,"E35.filletArc")])]})])],"derivedFrom":makeQuery(id+"F5.opExtrude","CAP_EDGE",EDGE,{"disambiguationData":[OSD([subQ0])],"isStart":false})});}
            var Q4;
            {var subQ0=sQuery(id+"F0.wireOp",EDGE,"E25.7");var subQ1=sQuery(id+"F0.wireOp",EDGE,"E25.1");var subQ2=sQuery(id+"F0.wireOp",EDGE,"E25.6");var subQ3=sQuery(id+"F0.wireOp",EDGE,"E25.5");var subQ4=sQuery(id+"F0.wireOp",EDGE,"E25.4");var subQ5=sQuery(id+"F0.wireOp",EDGE,"E25.0");var subQ6=sQuery(id+"F0.wireOp",EDGE,"E25.2");var subQ7=sQuery(id+"F0.wireOp",EDGE,"E25.3");Q4=makeQuery(id+"F8.boolean.opBoolean","INTERSECT",EDGE,{"derivedFrom":[makeQuery(id+"F5.boolean.opBoolean","SPLIT",FACE,{"disambiguationData":[TD([makeQuery(id+"F2.opExtrude","SWEPT_FACE",FACE,{"disambiguationData":[OSD([subQ5])]})])],"derivedFrom":makeQuery(id+"F3.boolean.opBoolean","COPY",FACE,{"derivedFrom":makeQuery(id+"F3.opExtrude","CAP_FACE",FACE,{"disambiguationData":[OSD([subQ5,subQ1,subQ6,subQ7,subQ4,subQ3,subQ2,subQ0])],"isStart":false})})}),makeQuery(id+"F8.opExtrude","SWEPT_FACE",FACE,{"disambiguationData":[OSD([sQuery(id+"F7.wireOp",EDGE,"E67")])]})]});}
            var Q5;
            Q5=makeQuery(id+"F8.boolean.opBoolean","INTERSECT",EDGE,{"disambiguationData":[OD(0.0)],"derivedFrom":[makeQuery(id+"F5.opExtrude","SWEPT_FACE",FACE,{"disambiguationData":[OSD([sQuery(id+"F4.wireOp",EDGE,"E30")])]}),makeQuery(id+"F8.opExtrude","SWEPT_FACE",FACE,{"disambiguationData":[OSD([sQuery(id+"F7.wireOp",EDGE,"E67")])]})]});
            fillet(context, id + "F14", {"entities" : qUnion([Q0, Q1, Q2, Q3, Q4, Q5]), "radius" : 3 * mm, "tangentPropagation" : true, "allowEdgeOverflow" : false});
        }
        {
            var Q0;
            Q0=makeQuery(id+"F1.opExtrude","CAP_EDGE",EDGE,{"disambiguationData":[OSD([sQuery(id+"F0.wireOp",EDGE,"E1.bottom")])],"isStart":false});
            fillet(context, id + "F15", {"entities" : qUnion([Q0]), "radius" : 2 * mm, "tangentPropagation" : true, "allowEdgeOverflow" : false});
        }
        {
            var Q0;
            {var subQ0=sQuery(id+"F0.wireOp",EDGE,"E1.bottom");var subQ1=sQuery(id+"F0.wireOp",EDGE,"E1.top");var subQ2=sQuery(id+"F0.wireOp",EDGE,"E1.left");var subQ3=sQuery(id+"F0.wireOp",EDGE,"E1.right");var subQ4=sQuery(id+"F0.wireOp",EDGE,"E4");var subQ5=sQuery(id+"F0.wireOp",EDGE,"E5");var subQ6=sQuery(id+"F0.wireOp",EDGE,"E6");var subQ7=sQuery(id+"F0.wireOp",EDGE,"E7");var subQ8=sQuery(id+"F0.wireOp",EDGE,"E21.filletArc");var subQ9=sQuery(id+"F0.wireOp",EDGE,"E22.filletArc");var subQ10=sQuery(id+"F0.wireOp",EDGE,"E23.filletArc");var subQ11=sQuery(id+"F0.wireOp",EDGE,"E24.filletArc");Q0=makeQuery(id+"F2.boolean.opBoolean","SPLIT",FACE,{"disambiguationData":[TD([makeQuery(id+"F1.opExtrude","SWEPT_FACE",FACE,{"disambiguationData":[OSD([subQ0])]})])],"derivedFrom":makeQuery(id+"F1.opExtrude","CAP_FACE",FACE,{"disambiguationData":[OSD([subQ0,subQ1,subQ2,subQ3,subQ4,subQ5,subQ6,subQ7,subQ8,subQ9,subQ10,subQ11])],"isStart":true})});}
            var sketch = newSketch(context, id + "F16", { "sketchPlane" : qUnion([Q0])});
            skLineSegment(sketch, "E79.0", {"start": v(24.05, 208.38) * mm, "end": v(164.05, 208.38) * mm});
            skArc(sketch, "E79.1", {"start": v(24.05, 208.38) * mm, "mid": v(16.98, 205.45) * mm, "end": v(14.05, 198.38) * mm});
            skLineSegment(sketch, "E79.2", {"start": v(14.05, 38.38) * mm, "end": v(14.05, 198.38) * mm});
            skArc(sketch, "E79.3", {"start": v(14.05, 38.38) * mm, "mid": v(16.98, 31.31) * mm, "end": v(24.05, 28.38) * mm});
            skLineSegment(sketch, "E79.4", {"start": v(24.05, 28.38) * mm, "end": v(164.05, 28.38) * mm});
            skArc(sketch, "E79.5", {"start": v(164.05, 28.38) * mm, "mid": v(171.12, 31.31) * mm, "end": v(174.05, 38.38) * mm});
            skLineSegment(sketch, "E79.6", {"start": v(174.05, 38.38) * mm, "end": v(174.05, 198.38) * mm});
            skArc(sketch, "E79.7", {"start": v(174.05, 198.38) * mm, "mid": v(171.12, 205.45) * mm, "end": v(164.05, 208.38) * mm});
            skCircle(sketch, "E79.8", {"center": v(34.05, 185.88) * mm, "radius": 4 * mm});
            skCircle(sketch, "E79.9", {"center": v(154.05, 185.88) * mm, "radius": 4 * mm});
            skCircle(sketch, "E79.10", {"center": v(34.05, 50.88) * mm, "radius": 4 * mm});
            skCircle(sketch, "E79.11", {"center": v(154.05, 50.88) * mm, "radius": 4 * mm});
            skArc(sketch, "E79.12", {"start": v(150.2, 166.56) * mm, "mid": v(94.05, 185.88) * mm, "end": v(37.9, 166.56) * mm});
            skArc(sketch, "E79.13", {"start": v(37.9, 166.56) * mm, "mid": v(35.06, 163.06) * mm, "end": v(34.05, 158.68) * mm});
            skLineSegment(sketch, "E79.14", {"start": v(34.05, 158.68) * mm, "end": v(34.05, 78.09) * mm});
            skArc(sketch, "E79.15", {"start": v(34.05, 78.09) * mm, "mid": v(35.06, 73.7) * mm, "end": v(37.9, 70.2) * mm});
            skArc(sketch, "E79.16", {"start": v(37.9, 70.2) * mm, "mid": v(94.05, 50.88) * mm, "end": v(150.2, 70.2) * mm});
            skArc(sketch, "E79.17", {"start": v(150.2, 70.2) * mm, "mid": v(153.04, 73.7) * mm, "end": v(154.05, 78.09) * mm});
            skLineSegment(sketch, "E79.18", {"start": v(154.05, 158.68) * mm, "end": v(154.05, 78.09) * mm});
            skArc(sketch, "E79.19", {"start": v(154.05, 158.68) * mm, "mid": v(153.04, 163.06) * mm, "end": v(150.2, 166.56) * mm});
            skLineSegment(sketch, "E80", {"start": v(94.05, 208.38) * mm, "end": v(94.05, 238.38) * mm, "construction": true});
            skLineSegment(sketch, "E81", {"start": v(61.05, 208.38) * mm, "end": v(79.05, 226.38) * mm});
            skLineSegment(sketch, "E82", {"start": v(79.05, 226.38) * mm, "end": v(79.05, 238.38) * mm});
            skLineSegment(sketch, "E83", {"start": v(127.05, 208.38) * mm, "end": v(109.05, 226.38) * mm});
            skLineSegment(sketch, "E84", {"start": v(109.05, 226.38) * mm, "end": v(109.05, 238.38) * mm});
            skArc(sketch, "E85", {"start": v(109.05, 238.38) * mm, "mid": v(94.05, 253.38) * mm, "end": v(79.05, 238.38) * mm});
            skCircle(sketch, "E86", {"center": v(94.05, 238.38) * mm, "radius": 6 * mm});
            skLineSegment(sketch, "E87", {"start": v(14.05, 118.38) * mm, "end": v(174.05, 118.38) * mm, "construction": true});
            skLineSegment(sketch, "E88.MirrorCS", {"start": v(109.05, 10.38) * mm, "end": v(109.05, -1.62) * mm});
            skLineSegment(sketch, "E89.MirrorCS", {"start": v(79.05, 10.38) * mm, "end": v(79.05, -1.62) * mm});
            skLineSegment(sketch, "E90.MirrorCS", {"start": v(127.05, 28.38) * mm, "end": v(109.05, 10.38) * mm});
            skCircle(sketch, "E91.MirrorC", {"center": v(94.05, -1.62) * mm, "radius": 6 * mm});
            skLineSegment(sketch, "E92.MirrorCS", {"start": v(94.05, 28.38) * mm, "end": v(94.05, -1.62) * mm});
            skLineSegment(sketch, "E93.MirrorCS", {"start": v(61.05, 28.38) * mm, "end": v(79.05, 10.38) * mm});
            skArc(sketch, "E94.MirrorCS", {"start": v(109.05, -1.62) * mm, "mid": v(94.05, -16.62) * mm, "end": v(79.05, -1.62) * mm});
            skSolve(sketch);
        }
        {
            var Q0;
            Q0 = qSketchRegion(id + "F16", true);
            var Q1;
            Q1=makeQuery(id+"F2.opExtrude","CAP_FACE",FACE,{"disambiguationData":[OSD([sQuery(id+"F0.wireOp",EDGE,"E12"),sQuery(id+"F0.wireOp",EDGE,"E13"),sQuery(id+"F0.wireOp",EDGE,"E14"),sQuery(id+"F0.wireOp",EDGE,"E15"),sQuery(id+"F0.wireOp",EDGE,"E17.filletArc"),sQuery(id+"F0.wireOp",EDGE,"E18.filletArc"),sQuery(id+"F0.wireOp",EDGE,"E19.filletArc"),sQuery(id+"F0.wireOp",EDGE,"E20.filletArc"),sQuery(id+"F0.wireOp",EDGE,"E25.0"),sQuery(id+"F0.wireOp",EDGE,"E25.1"),sQuery(id+"F0.wireOp",EDGE,"E25.2"),sQuery(id+"F0.wireOp",EDGE,"E25.3"),sQuery(id+"F0.wireOp",EDGE,"E25.4"),sQuery(id+"F0.wireOp",EDGE,"E25.5"),sQuery(id+"F0.wireOp",EDGE,"E25.6"),sQuery(id+"F0.wireOp",EDGE,"E25.7")])],"isStart":false});
            extrude(context, id + "F17", {"entities" : qUnion([Q0]), "operationType" : NewBodyOperationType.ADD, "endBound" : BoundingType.UP_TO_SURFACE, "endBoundEntityFace" : qUnion([Q1]), "depth" : 25 * mm});
        }
    });
